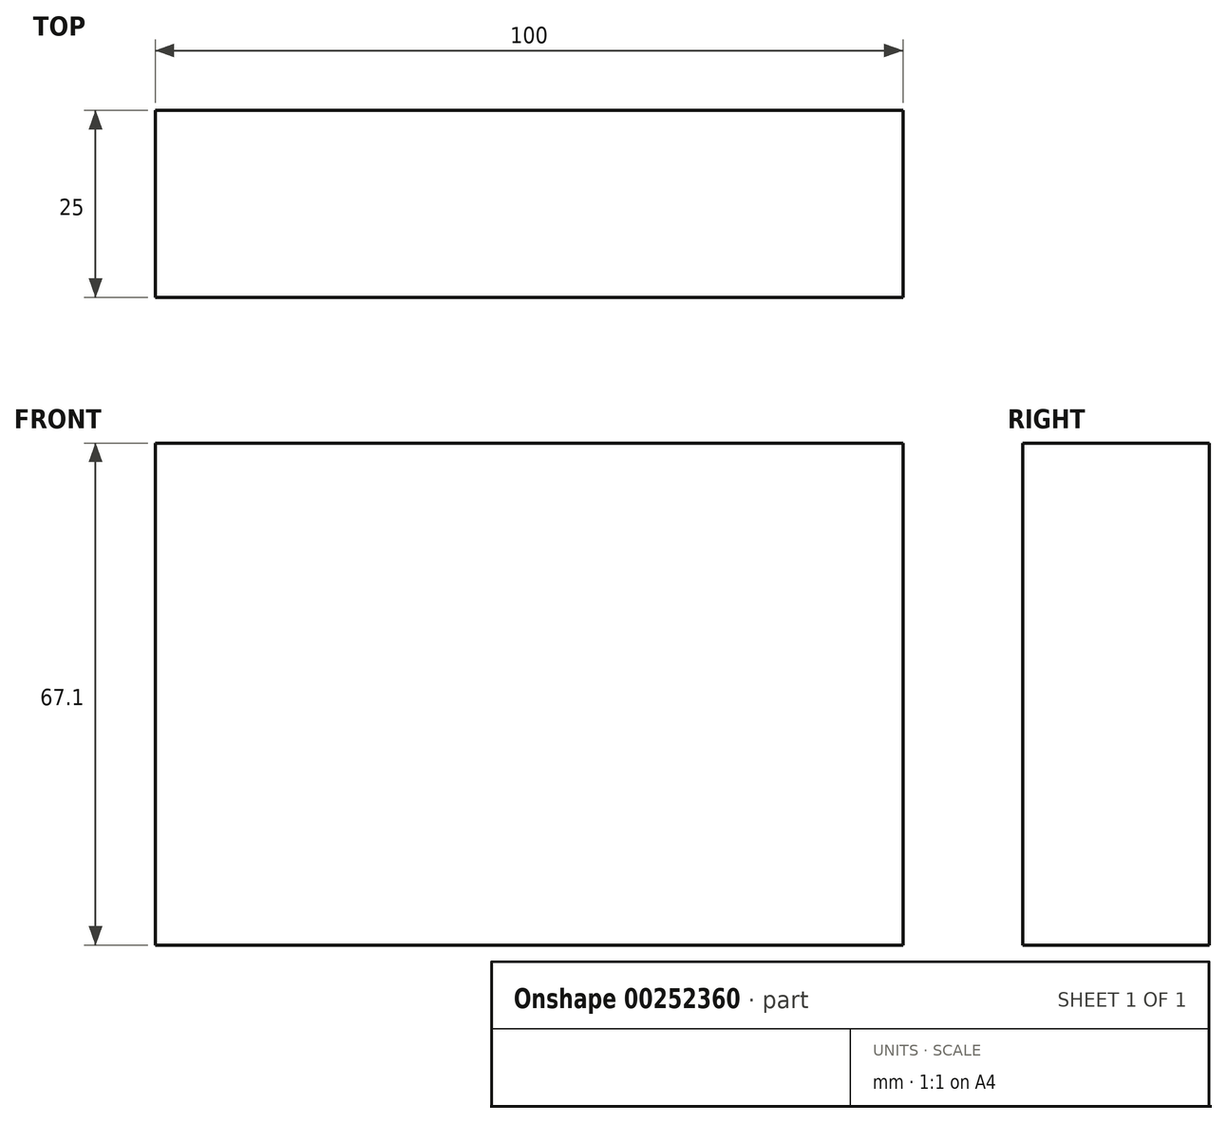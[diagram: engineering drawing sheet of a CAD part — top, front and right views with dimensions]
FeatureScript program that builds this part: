
annotation { "Feature Type Name" : "Feature", "Feature Type Description" : "" }
export const myFeature = defineFeature(function(context is Context, id is Id, definition is map)
    precondition{}
    {
        {
            var Q0;
            Q0=qCreatedBy(makeId("Front.planeOp"),FACE);
            var sketch = newSketch(context, id + "F0", { "sketchPlane" : qUnion([Q0])});
            skLineSegment(sketch, "E0.bottom", {"start": v(-54.3, 49.66) * mm, "end": v(45.7, 49.66) * mm});
            skLineSegment(sketch, "E0.top", {"start": v(-54.3, -17.44) * mm, "end": v(45.7, -17.44) * mm});
            skLineSegment(sketch, "E0.left", {"start": v(-54.3, 49.66) * mm, "end": v(-54.3, -17.44) * mm});
            skLineSegment(sketch, "E0.right", {"start": v(45.7, 49.66) * mm, "end": v(45.7, -17.44) * mm});
            skPoint(sketch, "E0.middle", {"position": v(-4.3, 16.11) * mm});
            skSolve(sketch);
        }
        {
            var Q0;
            Q0 = qSketchRegion(id + "F0", true);
            extrude(context, id + "F1", {"entities" : qUnion([Q0]), "depth" : 25 * mm});
        }
    });
